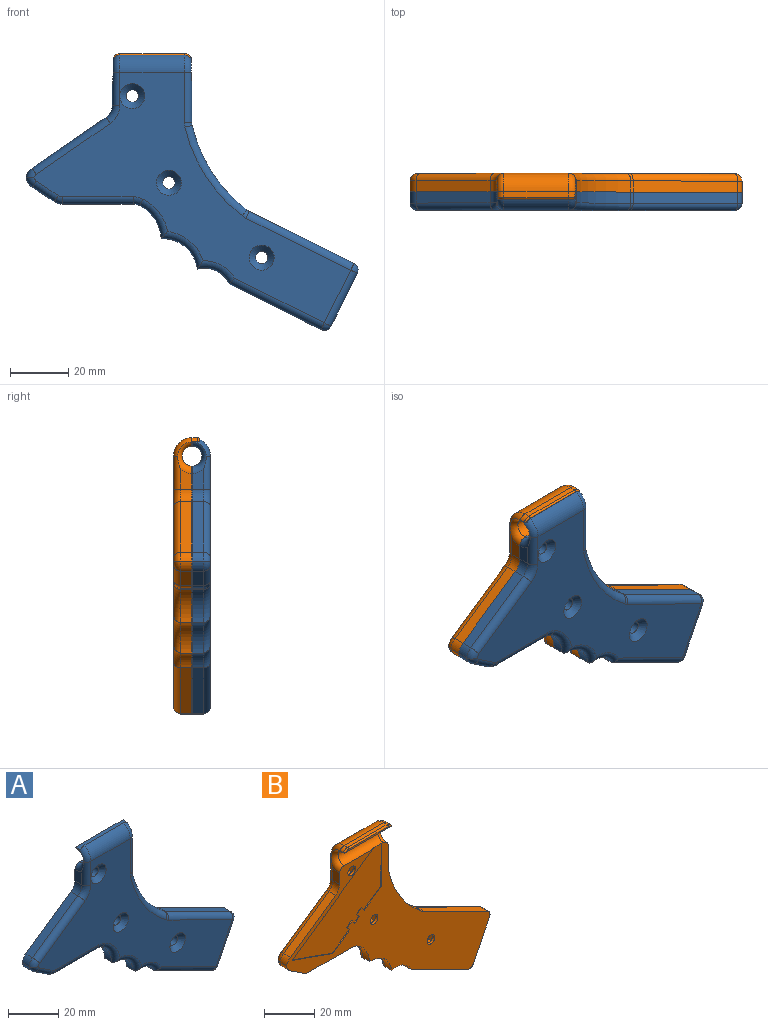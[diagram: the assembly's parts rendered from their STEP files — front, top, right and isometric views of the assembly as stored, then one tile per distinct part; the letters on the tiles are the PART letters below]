
ASSEMBLY  parts=2 mates=1
PART A: 72 faces, bbox 114.7x8.4x97.3 mm
  f0: plane 26.83x1.46mm, normal (0,1,0), area 37.3mm2, adj f8,f37,f61,f70
  f1: cylinder r=6.35mm len=22.23mm, axis (-1,0,0), area 163.6mm2, adj f7,f38,f63,f71
  f2: cylinder r=12.12mm len=12.47mm, axis (0,1,0), area 68mm2, adj f4,f27,f29,f49
  f3: plane 7.51x5mm, normal (-0.55,0,-0.83), area 34.4mm2, adj f4,f30,f33,f44
  f4: plane 114.31x85.46mm, normal (0,1,0), area 2541.7mm2, adj f2,f3,f5,f6,f8,f9,f10,f11
  f5: plane 12.62x3.81mm, normal (1,0,0), area 44.5mm2, adj f4,f35,f61,f62
  f6: plane 36.06x17.92mm, normal (0.44,0,0.9), area 153.4mm2, adj f4,f34,f54,f57
  f7: plane 109.14x86.35mm, normal (0,-1,0), area 2665.3mm2, adj f1,f39,f40,f41,f42,f43,f44,f45
  f8: cylinder r=3.43mm len=22.23mm, axis (-1,0,0), area 237.9mm2, adj f0,f4,f9,f10,f21,f37,f61
  f9: plane 45.61x31.58mm, normal (0.57,0,-0.82), area 16.9mm2, adj f4,f8,f20,f21
  f10: plane 20.71x0.42mm, normal (-1,0,0.02), area 6.3mm2, adj f4,f8,f11,f21
  f11: plane 9.61x6.65mm, normal (-0.57,0,0.82), area 3.6mm2, adj f4,f10,f12,f21
  f12: plane 1.88x1.3mm, normal (0.82,0,0.57), area 0.7mm2, adj f4,f11,f13,f21
  f13: plane 2.72x1.88mm, normal (-0.57,0,0.82), area 1mm2, adj f4,f12,f14,f21
  f14: plane 1.88x1.3mm, normal (-0.82,0,-0.57), area 0.7mm2, adj f4,f13,f15,f21
  f15: plane 2.72x1.88mm, normal (-0.57,0,0.82), area 1mm2, adj f4,f14,f16,f21
  f16: plane 1.88x1.3mm, normal (0.82,0,0.57), area 0.7mm2, adj f4,f15,f17,f21
  f17: plane 2.66x1.84mm, normal (-0.57,0,0.82), area 1mm2, adj f4,f16,f18,f21
  f18: plane 1.88x1.3mm, normal (-0.82,0,-0.57), area 0.7mm2, adj f4,f17,f19,f21
  f19: plane 9.61x6.65mm, normal (-0.57,0,0.82), area 3.6mm2, adj f4,f18,f20,f21
  f20: plane 22.75x8.04mm, normal (0.33,0,0.94), area 7.4mm2, adj f4,f9,f19,f21
  f21: plane 50.47x39.61mm, normal (0,1,0), area 902.5mm2, adj f8,f9,f10,f11,f12,f13,f14,f15
  f22: plane 6.79x3.81mm, normal (-1,0,0), area 22.3mm2, adj f4,f36,f37,f39
  f23: plane 25.44x17.48mm, normal (-0.57,0,0.82), area 117.6mm2, adj f4,f32,f36,f41
  f24: plane 18.2x9.04mm, normal (0.9,0,-0.44), area 77.4mm2, adj f4,f51,f54,f55
  f25: plane 31.66x15.73mm, normal (-0.44,0,-0.9), area 134.7mm2, adj f4,f29,f51,f52
  f26: cylinder r=50.91mm len=29.1mm, axis (0,1,0), area 134.7mm2, adj f4,f34,f35,f59
  f27: cylinder r=13.38mm len=11.34mm, axis (0,1,0), area 54mm2, adj f2,f4,f31,f48
  f28: plane 24.39x3.81mm, normal (0,0,-1), area 92.9mm2, adj f4,f30,f31,f46
  f29: cylinder r=9.44mm len=10.92mm, axis (0,1,0), area 49.8mm2, adj f2,f4,f25,f50
  f30: cylinder r=5.08mm len=3.81mm, axis (0,-1,0), area 11.4mm2, adj f3,f4,f28,f45
  f31: cylinder r=5.08mm len=3.81mm, axis (0,1,0), area 9mm2, adj f4,f27,f28,f47
  f32: cylinder r=5.08mm len=3.81mm, axis (0,-1,0), area 15.2mm2, adj f4,f23,f33,f42
  f33: cylinder r=5.08mm len=3.81mm, axis (0,1,0), area 15.5mm2, adj f3,f4,f32,f43
  f34: cylinder r=5.08mm len=3.81mm, axis (0,1,0), area 3.6mm2, adj f4,f6,f26,f58
  f35: cylinder r=5.08mm len=3.81mm, axis (0,1,0), area 4.4mm2, adj f4,f5,f26,f60
  f36: cylinder r=5.08mm len=4.19mm, axis (0,1,0), area 18.8mm2, adj f4,f22,f23,f40
  f37: torus R=5.97mm, axis (1,0,0), area 41.4mm2, adj f0,f4,f8,f22,f38,f39
  f38: torus R=3.81mm, axis (1,0,0), area 19.5mm2, adj f1,f37,f39,f70,f71
  f39: cylinder r=2.54mm len=11.38mm, axis (0,0,-1), area 42mm2, adj f7,f22,f37,f38,f40
  f40: torus R=7.62mm, axis (0,-1,0), area 23.2mm2, adj f7,f36,f39,f41
  f41: cylinder r=2.54mm len=26.88mm, axis (-0.82,0,-0.57), area 123.1mm2, adj f7,f23,f40,f42
  f42: torus R=2.54mm, axis (0,-1,0), area 12.3mm2, adj f7,f32,f41,f43
  f43: torus R=2.54mm, axis (0,-1,0), area 12.6mm2, adj f7,f33,f42,f44
  f44: cylinder r=2.54mm len=8.91mm, axis (0.83,0,-0.55), area 36mm2, adj f3,f7,f43,f45
  f45: torus R=2.54mm, axis (0,-1,0), area 9.7mm2, adj f7,f30,f44,f46
  f46: cylinder r=2.54mm len=24.39mm, axis (1,0,0), area 97.3mm2, adj f7,f28,f45,f47
  f47: torus R=7.62mm, axis (0,-1,0), area 11.1mm2, adj f7,f31,f46,f48
  f48: torus R=15.92mm, axis (0,-1,0), area 57mm2, adj f7,f27,f47,f49
  f49: torus R=14.66mm, axis (0,-1,0), area 69.3mm2, adj f2,f7,f48,f50
  f50: torus R=11.98mm, axis (0,-1,0), area 52.1mm2, adj f7,f29,f49,f52
  f51: cylinder r=2.54mm len=3.81mm, axis (0,1,0), area 15.2mm2, adj f4,f24,f25,f53
  f52: cylinder r=2.54mm len=32.79mm, axis (-0.9,0,0.44), area 139.8mm2, adj f7,f25,f50,f53
  f53: sphere r=2.54mm, area 10.1mm2, adj f51,f52,f55
  f54: cylinder r=2.54mm len=3.81mm, axis (0,1,0), area 15.2mm2, adj f4,f6,f24,f56
  f55: cylinder r=2.54mm len=19.33mm, axis (-0.44,0,-0.9), area 81.1mm2, adj f7,f24,f53,f56
  f56: sphere r=2.54mm, area 10.1mm2, adj f54,f55,f57
  f57: cylinder r=2.54mm len=37.19mm, axis (0.9,0,-0.44), area 160.6mm2, adj f6,f7,f56,f58
  f58: torus R=7.62mm, axis (0,-1,0), area 4.5mm2, adj f7,f34,f57,f59
  f59: torus R=53.45mm, axis (0,-1,0), area 143.7mm2, adj f7,f26,f58,f60
  f60: torus R=7.62mm, axis (0,-1,0), area 5.4mm2, adj f7,f35,f59,f62
  f61: torus R=5.97mm, axis (1,0,0), area 41.4mm2, adj f0,f4,f5,f8,f62,f63
  f62: cylinder r=2.54mm len=17.22mm, axis (0,0,1), area 65.3mm2, adj f5,f7,f60,f61,f63
  f63: torus R=3.81mm, axis (1,0,0), area 19.5mm2, adj f1,f61,f62,f70,f71
  f64: cylinder r=2.16mm len=4.32mm, axis (0,-1,0), area 56.9mm2, adj f4,f65
  f65: cone r=2.16mm half-angle=45deg, axis (0,-1,0), area 62.1mm2, adj f7,f64
  f66: cylinder r=2.16mm len=4.32mm, axis (0,-1,0), area 56.9mm2, adj f4,f67
  f67: cone r=2.16mm half-angle=45deg, axis (0,-1,0), area 62.1mm2, adj f7,f66
  f68: cylinder r=2.16mm len=4.32mm, axis (0,-1,0), area 56.9mm2, adj f4,f69
  f69: cone r=2.16mm half-angle=45deg, axis (0,-1,0), area 62.1mm2, adj f7,f68
  f70: plane 26.83x2.54mm, normal (0,0,1), area 67.5mm2, adj f0,f38,f63,f71
  f71: plane 26x0.93mm, normal (0,1,0), area 23.1mm2, adj f1,f38,f63,f70
PART B: 96 faces, bbox 114.7x11x97.3 mm
  f0: plane 26.83x1.46mm, normal (0,-1,0), area 37.3mm2, adj f10,f40,f64,f89
  f1: cylinder r=2.16mm len=4.32mm, axis (0,1,0), area 17.2mm2, adj f6,f87
  f2: cylinder r=2.16mm len=4.32mm, axis (0,1,0), area 17.2mm2, adj f6,f80
  f3: cylinder r=2.16mm len=4.32mm, axis (0,1,0), area 17.2mm2, adj f6,f73
  f4: cylinder r=12.12mm len=12.47mm, axis (0,-1,0), area 68mm2, adj f6,f30,f32,f52
  f5: plane 7.51x5mm, normal (-0.55,0,-0.83), area 34.4mm2, adj f6,f33,f36,f47
  f6: plane 114.31x85.46mm, normal (0,-1,0), area 2541.7mm2, adj f1,f2,f3,f4,f5,f7,f8,f10
  f7: plane 12.62x3.81mm, normal (1,0,0), area 44.5mm2, adj f6,f38,f64,f65
  f8: plane 36.06x17.92mm, normal (0.44,0,0.9), area 153.4mm2, adj f6,f37,f57,f60
  f9: plane 109.14x86.35mm, normal (0,1,0), area 2647.9mm2, adj f11,f42,f43,f44,f45,f46,f47,f48
  f10: cylinder r=3.43mm len=22.23mm, axis (-1,0,0), area 237.9mm2, adj f0,f6,f12,f13,f24,f40,f64
  f11: cylinder r=6.35mm len=22.23mm, axis (-1,0,0), area 221.7mm2, adj f9,f41,f66,f91
  f12: plane 45.61x31.58mm, normal (0.57,0,-0.82), area 16.9mm2, adj f6,f10,f23,f24
  f13: plane 20.71x0.42mm, normal (-1,0,0.02), area 6.3mm2, adj f6,f10,f14,f24
  f14: plane 9.61x6.65mm, normal (-0.57,0,0.82), area 3.6mm2, adj f6,f13,f15,f24
  f15: plane 1.88x1.3mm, normal (0.82,0,0.57), area 0.7mm2, adj f6,f14,f16,f24
  f16: plane 2.72x1.88mm, normal (-0.57,0,0.82), area 1mm2, adj f6,f15,f17,f24
  f17: plane 1.88x1.3mm, normal (-0.82,0,-0.57), area 0.7mm2, adj f6,f16,f18,f24
  f18: plane 2.72x1.88mm, normal (-0.57,0,0.82), area 1mm2, adj f6,f17,f19,f24
  f19: plane 1.88x1.3mm, normal (0.82,0,0.57), area 0.7mm2, adj f6,f18,f20,f24
  f20: plane 2.66x1.84mm, normal (-0.57,0,0.82), area 1mm2, adj f6,f19,f21,f24
  f21: plane 1.88x1.3mm, normal (-0.82,0,-0.57), area 0.7mm2, adj f6,f20,f22,f24
  f22: plane 9.61x6.65mm, normal (-0.57,0,0.82), area 3.6mm2, adj f6,f21,f23,f24
  f23: plane 22.75x8.04mm, normal (0.33,0,0.94), area 7.4mm2, adj f6,f12,f22,f24
  f24: plane 50.47x39.61mm, normal (0,-1,0), area 902.5mm2, adj f10,f12,f13,f14,f15,f16,f17,f18
  f25: plane 6.79x3.81mm, normal (-1,0,0), area 22.3mm2, adj f6,f39,f40,f42
  f26: plane 25.44x17.48mm, normal (-0.57,0,0.82), area 117.6mm2, adj f6,f35,f39,f44
  f27: plane 18.2x9.04mm, normal (0.9,0,-0.44), area 77.4mm2, adj f6,f54,f57,f58
  f28: plane 31.66x15.73mm, normal (-0.44,0,-0.9), area 134.7mm2, adj f6,f32,f54,f55
  f29: cylinder r=50.91mm len=29.1mm, axis (0,-1,0), area 134.7mm2, adj f6,f37,f38,f62
  f30: cylinder r=13.38mm len=11.34mm, axis (0,-1,0), area 54mm2, adj f4,f6,f34,f51
  f31: plane 24.39x3.81mm, normal (0,0,-1), area 92.9mm2, adj f6,f33,f34,f49
  f32: cylinder r=9.44mm len=10.92mm, axis (0,-1,0), area 49.8mm2, adj f4,f6,f28,f53
  f33: cylinder r=5.08mm len=3.81mm, axis (0,1,0), area 11.4mm2, adj f5,f6,f31,f48
  f34: cylinder r=5.08mm len=3.81mm, axis (0,-1,0), area 9mm2, adj f6,f30,f31,f50
  f35: cylinder r=5.08mm len=3.81mm, axis (0,1,0), area 15.2mm2, adj f6,f26,f36,f45
  f36: cylinder r=5.08mm len=3.81mm, axis (0,-1,0), area 15.5mm2, adj f5,f6,f35,f46
  f37: cylinder r=5.08mm len=3.81mm, axis (0,-1,0), area 3.6mm2, adj f6,f8,f29,f61
  f38: cylinder r=5.08mm len=3.81mm, axis (0,-1,0), area 4.4mm2, adj f6,f7,f29,f63
  f39: cylinder r=5.08mm len=4.19mm, axis (0,-1,0), area 18.8mm2, adj f6,f25,f26,f43
  f40: torus R=5.97mm, axis (1,0,0), area 41.4mm2, adj f0,f6,f10,f25,f41,f42
  f41: torus R=3.81mm, axis (1,0,0), area 26.4mm2, adj f11,f40,f42,f88
  f42: cylinder r=2.54mm len=11.38mm, axis (0,0,-1), area 41.4mm2, adj f9,f25,f40,f41,f43,f67,f72
  f43: torus R=7.62mm, axis (0,1,0), area 23.2mm2, adj f9,f39,f42,f44
  f44: cylinder r=2.54mm len=26.88mm, axis (-0.82,0,-0.57), area 123.1mm2, adj f9,f26,f43,f45
  f45: torus R=2.54mm, axis (0,1,0), area 12.3mm2, adj f9,f35,f44,f46
  f46: torus R=2.54mm, axis (0,1,0), area 12.6mm2, adj f9,f36,f45,f47
  f47: cylinder r=2.54mm len=8.91mm, axis (0.83,0,-0.55), area 36mm2, adj f5,f9,f46,f48
  f48: torus R=2.54mm, axis (0,1,0), area 9.7mm2, adj f9,f33,f47,f49
  f49: cylinder r=2.54mm len=24.39mm, axis (1,0,0), area 97.3mm2, adj f9,f31,f48,f50
  f50: torus R=7.62mm, axis (0,1,0), area 11.1mm2, adj f9,f34,f49,f51
  f51: torus R=15.92mm, axis (0,1,0), area 57mm2, adj f9,f30,f50,f52
  f52: torus R=14.66mm, axis (0,1,0), area 69.3mm2, adj f4,f9,f51,f53
  f53: torus R=11.98mm, axis (0,1,0), area 52.1mm2, adj f9,f32,f52,f55
  f54: cylinder r=2.54mm len=3.81mm, axis (0,-1,0), area 15.2mm2, adj f6,f27,f28,f56
  f55: cylinder r=2.54mm len=32.79mm, axis (-0.9,0,0.44), area 139.8mm2, adj f9,f28,f53,f56
  f56: sphere r=2.54mm, area 10.1mm2, adj f54,f55,f58
  f57: cylinder r=2.54mm len=3.81mm, axis (0,-1,0), area 15.2mm2, adj f6,f8,f27,f59
  f58: cylinder r=2.54mm len=19.33mm, axis (-0.44,0,-0.9), area 81.1mm2, adj f9,f27,f56,f59
  f59: sphere r=2.54mm, area 10.1mm2, adj f57,f58,f60
  f60: cylinder r=2.54mm len=37.19mm, axis (0.9,0,-0.44), area 160.6mm2, adj f8,f9,f59,f61
  f61: torus R=7.62mm, axis (0,1,0), area 4.5mm2, adj f9,f37,f60,f62
  f62: torus R=53.45mm, axis (0,1,0), area 143.7mm2, adj f9,f29,f61,f63
  f63: torus R=7.62mm, axis (0,1,0), area 5.4mm2, adj f9,f38,f62,f65
  f64: torus R=5.97mm, axis (1,0,0), area 41.4mm2, adj f0,f6,f7,f10,f65,f66
  f65: cylinder r=2.54mm len=17.22mm, axis (0,0,1), area 65.3mm2, adj f7,f9,f63,f64,f66
  f66: torus R=3.81mm, axis (1,0,0), area 26.4mm2, adj f11,f64,f65,f90
  f67: plane 5.09x4.73mm, normal (0.95,0,-0.32), area 25.3mm2, adj f9,f42,f68,f72,f73
  f68: plane 5.08x4.89mm, normal (0.2,0,-0.98), area 25.3mm2, adj f9,f67,f69,f73
  f69: plane 5.08x3.75mm, normal (-0.75,0,-0.66), area 25.3mm2, adj f9,f68,f70,f73
  f70: plane 5.08x4.72mm, normal (-0.95,0,0.32), area 25.3mm2, adj f9,f69,f71,f73
  f71: plane 5.08x4.89mm, normal (-0.2,0,0.98), area 25.3mm2, adj f9,f70,f72,f73
  f72: plane 5.08x3.75mm, normal (0.75,0,0.66), area 25.3mm2, adj f9,f42,f67,f71,f73
  f73: plane 9.78x9.44mm, normal (0,1,0), area 49.9mm2, adj f3,f67,f68,f69,f70,f71,f72
  f74: plane 5.08x3.75mm, normal (-0.75,0,-0.66), area 25.3mm2, adj f9,f75,f79,f80
  f75: plane 5.08x4.72mm, normal (-0.95,0,0.32), area 25.3mm2, adj f9,f74,f76,f80
  f76: plane 5.08x4.89mm, normal (-0.2,0,0.98), area 25.3mm2, adj f9,f75,f77,f80
  f77: plane 5.08x3.75mm, normal (0.75,0,0.66), area 25.3mm2, adj f9,f76,f78,f80
  f78: plane 5.08x4.72mm, normal (0.95,0,-0.32), area 25.3mm2, adj f9,f77,f79,f80
  f79: plane 5.08x4.89mm, normal (0.2,0,-0.98), area 25.3mm2, adj f9,f74,f78,f80
  f80: plane 9.78x9.44mm, normal (0,1,0), area 49.9mm2, adj f2,f74,f75,f76,f77,f78,f79
  f81: plane 5.08x4.72mm, normal (-0.95,0,0.32), area 25.3mm2, adj f9,f82,f86,f87
  f82: plane 5.08x4.89mm, normal (-0.2,0,0.98), area 25.3mm2, adj f9,f81,f83,f87
  f83: plane 5.08x3.75mm, normal (0.75,0,0.66), area 25.3mm2, adj f9,f82,f84,f87
  f84: plane 5.08x4.72mm, normal (0.95,0,-0.32), area 25.3mm2, adj f9,f83,f85,f87
  f85: plane 5.08x4.89mm, normal (0.2,0,-0.98), area 25.3mm2, adj f9,f84,f86,f87
  f86: plane 5.08x3.75mm, normal (-0.75,0,-0.66), area 25.3mm2, adj f9,f81,f85,f87
  f87: plane 9.78x9.44mm, normal (0,1,0), area 49.9mm2, adj f1,f81,f82,f83,f84,f85,f86
  f88: cylinder r=2.54mm len=2.3mm, axis (0,1,0), area 5.5mm2, adj f41,f89,f91,f93
  f89: plane 26.83x2.54mm, normal (0,0,-1), area 67.9mm2, adj f0,f88,f90,f92,f93,f95
  f90: cylinder r=2.54mm len=2.3mm, axis (0,1,0), area 5.5mm2, adj f66,f89,f91,f95
  f91: plane 22.23x1.91mm, normal (0,0,1), area 42.3mm2, adj f11,f88,f90,f94
  f92: plane 25.37x0.83mm, normal (0,-1,0), area 20.2mm2, adj f89,f93,f94,f95
  f93: torus R=1.91mm, axis (0,-1,0), area 2.5mm2, adj f88,f89,f92,f94
  f94: cylinder r=0.64mm len=22.23mm, axis (1,0,0), area 22.2mm2, adj f91,f92,f93,f95
  f95: torus R=1.91mm, axis (0,-1,0), area 2.5mm2, adj f89,f90,f92,f94
PLACE A at identity
PLACE B t=(0,-95.25,0)mm
MATE fastened B.f0 <-> A.f0  axis (0,-1,0) through (43.5,3.18,42.28)mm
